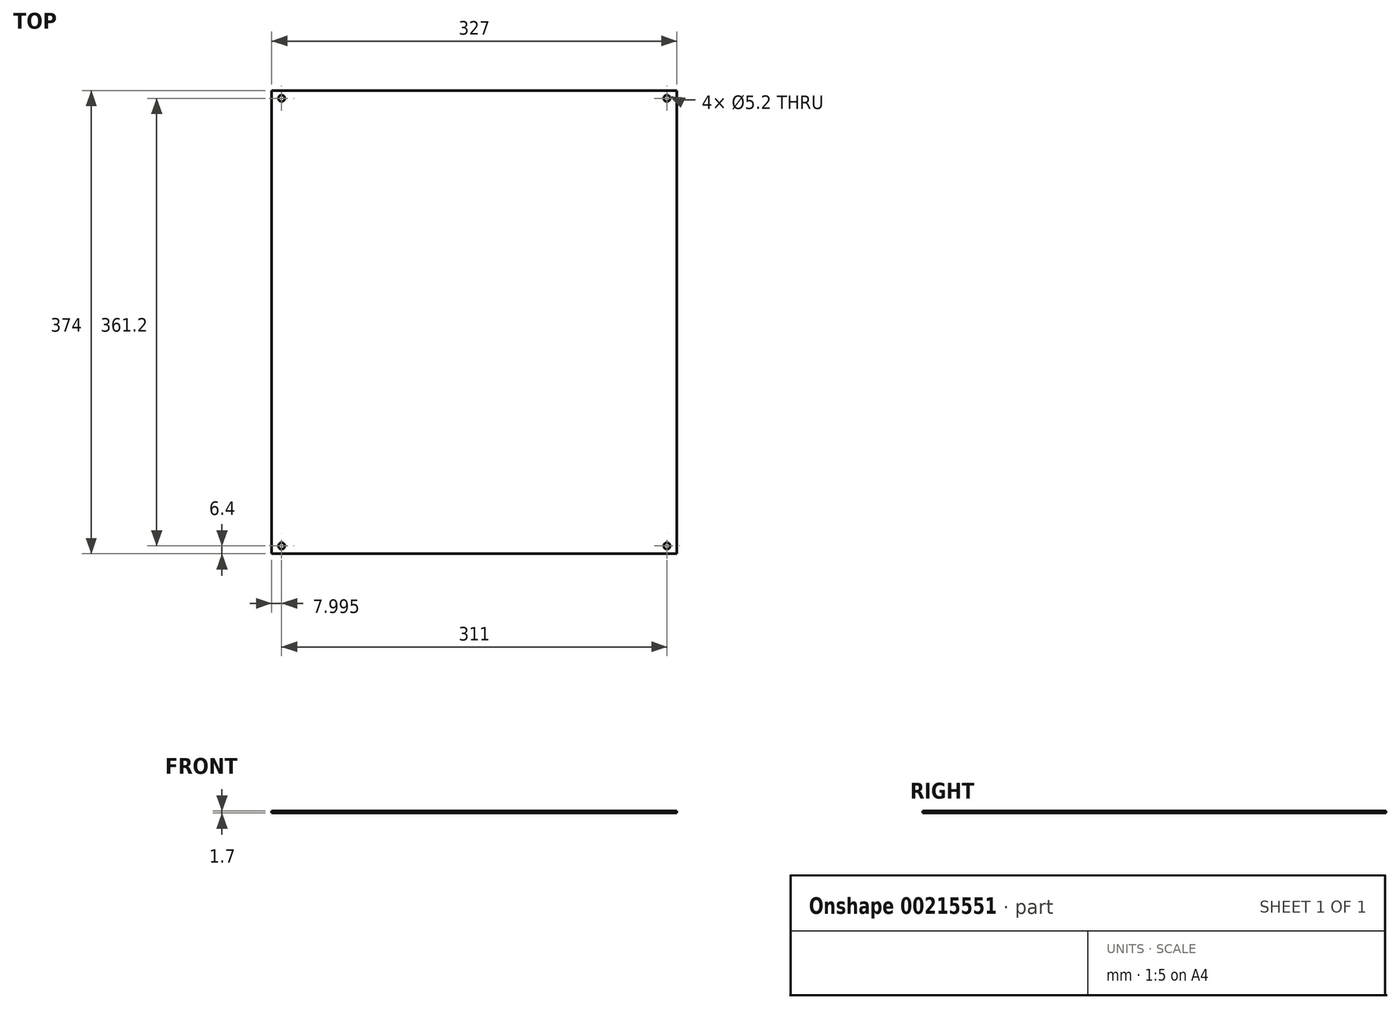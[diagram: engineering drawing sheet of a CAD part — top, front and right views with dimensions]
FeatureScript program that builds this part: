
annotation { "Feature Type Name" : "Feature", "Feature Type Description" : "" }
export const myFeature = defineFeature(function(context is Context, id is Id, definition is map)
    precondition{}
    {
        {
            var Q0;
            Q0=qCreatedBy(makeId("Top.planeOp"),FACE);
            var sketch = newSketch(context, id + "F0", { "sketchPlane" : qUnion([Q0])});
            skLineSegment(sketch, "E0.bottom", {"start": v(4.69, 0) * mm, "end": v(331.69, 0) * mm});
            skLineSegment(sketch, "E0.top", {"start": v(4.69, 374) * mm, "end": v(331.69, 374) * mm});
            skLineSegment(sketch, "E0.left", {"start": v(4.69, 0) * mm, "end": v(4.69, 374) * mm});
            skLineSegment(sketch, "E0.right", {"start": v(331.69, 0) * mm, "end": v(331.69, 374) * mm});
            skCircle(sketch, "E1", {"center": v(12.69, 6.4) * mm, "radius": 2.6 * mm});
            skCircle(sketch, "E2", {"center": v(12.69, 367.6) * mm, "radius": 2.6 * mm});
            skCircle(sketch, "E3", {"center": v(323.69, 6.4) * mm, "radius": 2.6 * mm});
            skCircle(sketch, "E4", {"center": v(323.69, 367.6) * mm, "radius": 2.6 * mm});
            skSolve(sketch);
        }
        {
            var Q0;
            Q0 = qSketchRegion(id + "F0", true);
            extrude(context, id + "F1", {"entities" : qUnion([Q0]), "depth" : 1.7 * mm});
        }
    });
